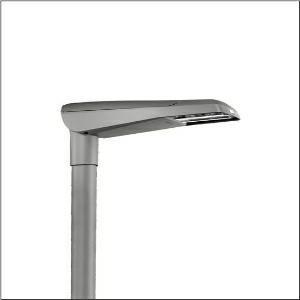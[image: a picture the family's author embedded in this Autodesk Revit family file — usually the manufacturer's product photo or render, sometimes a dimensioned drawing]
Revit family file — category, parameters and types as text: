
# Revit family: streetlight_sl_11_iq_micro___p1_0a_5xc1c51f08ce_61b4
name_source: partatom
category: Lighting Fixtures
units: mm (PartAtom-declared; Revit-internal decimal feet)

## family parameters
Cut with Voids When Loaded = No
Host = Face
Light Source = No
Part Type = Normal
Room Calculation Point = No
Round Connector Dimension = Use Diameter
Shared = No

## types (1)
- --- (1 x LED, 1600 lm, 10.8 W, 3000K)
    Apparent Load = 11 VA
    CIE Flux Codes = 29 63 93 100 100
    Color Rendering = 70
    Color Temperature = 3000K
    Default Elevation = 1800 mm
    Description = Streetlight SL 11 iQ micro, mast luminaire, primary light control with 3 zone facetted reflector, of plastic, silver coated, highly specular, primary optical cover: cover, of PMMA, transparent, light distribution: P1.0a, light emission: direct distribution, primary light characteristic: asymmetric, installation type: post-top, side-entry, lamps: LED, High Power LED, rated values: 1.600lm | 10,8W | 148,1lm/W (begin service life); end service life: 1.600lm | 11,1W; at 50% lumin. flux: 800lm | 6W | 133,3lm/W, colour temperature: 3000K, colour rendering: CRI > 70, light colour: 730, light setting 1 begin service life: 100% | 1.600lm | 10,8W | 148,1lm/W | 3.000K, light setting 1 end service life: 11,1W, further light settings possible, control: Street-Remote, optimised constant luminous flux control (CLO 2.0), Desk-Remote (wireless, voltage-free reading and setting of iQ features in the workshop via application-optimized NFC function/RFID function), Light-Fading, Smart-Wire, Night-Set, Lumen-Switch, Temp-Guard, Auto-Match, with cable H07RN-F 5x 1.5mm², mains connection: 230..240V, AC, 50/60Hz, connection cable pre-assembled, cable length: 5,5m, luminaire housing, of diecast aluminium, powder-coated, Siteco® metallic grey (DB 702S), please order mast flange separately, inclination adjustable without tools: 0°, 5°, 10°, 15° (post-top) | 0°, -5°, -10°, -15° (side-entry), sealing non-destructively replaceable, multi-level sealing system, length: 600mm, width: 174mm, height: 116mm, mast flange for spigot size: 42mm (side-entry): 5XC10008XM4, 60/48mm (side-entry/post-top): 5XC10108XM2, 76/60mm (side-entry/post-top): 5XC10108XM1, equipment: standard, protection rating (complete): IP66, insulation class (complete): insulation class II (safety insulation), certification: CE, ENEC, ENEC+, VDE, impact resistance: IK10, permissible operating ambient temperature for outdoor applications: -25..+50°C, standard-compliant lighting for roads and squares, Environmental Product Declaration (EPD) tested and certified by an independent institute, packaging unit: 1 piece

Light Distribution: P1.0a
    Height = 116 mm
    Lamp = 1 x LED
    Lamp Light Flux = 1600 lm
    Lamp Power = 10.8 W
    Lamp count = 1
    Length = 600 mm
    Luminous efficacy = 148 lm/W
    Manufacturer = Siteco
    ModVariant = No
    Model = 5XC1C51F08CE
    Number of Poles = 1
    OnlyDefault = Yes
    Power Factor = 1
    Product Name = Streetlight SL 11 iQ micro | P1.0a
    Product group = mast luminaire | pylon top
    ProductGroupID = 6100
    Protection Class = Protection class II
    Protection Degree = IP 66
    RLX_Detail_Level = 1
    RLX_Emergency_Light_Flux = 0 lm
    RLX_Emergency_Type = 0
    RLX_Emergency_Type_DB = No
    RlxData = <blob elided: 26645 chars, md5=f45b8869>
    Socket = socket
    Standby Power = 0 W
    System Light Flux = 1600 lm
    System Power = 11 W
    Type Comments = factory setting: luminous flux: 100 % | dim-lin: 254 | 194 mA
    Type Image = l_1006566.jpg
    URL = http://relux.com
    VarID = @adj_001095
    Voltage = 0 V
    Weight = 0.00 kg
    Width = 174 mm

## geometry (parser evidence)
native form markers: Blend x4, Sweep x10
no freeform markers — native parametric forms only
